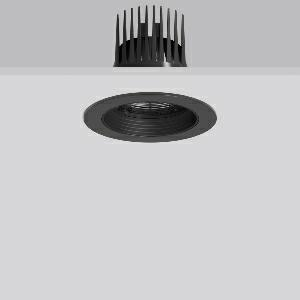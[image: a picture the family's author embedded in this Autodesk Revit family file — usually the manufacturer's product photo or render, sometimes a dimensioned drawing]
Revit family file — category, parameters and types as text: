
# Revit family: heledon_maxi_e_901767_003_1_8370
name_source: partatom
category: Lighting Fixtures
units: mm (PartAtom-declared; Revit-internal decimal feet)

## family parameters
Cut with Voids When Loaded = No
Host = Face
Light Source = No
Part Type = Normal
Room Calculation Point = No
Round Connector Dimension = Use Diameter
Shared = No

## types (1)
- HELEDON maxi E (1 x LED Modul 940, 3900 lm, 4000)
    Apparent Load = 35 VA
    Approval mark = CE
    CIE Flux Codes = 97 100 100 100 100
    Color Rendering = 92
    Color Temperature = 4000
    Default Elevation = 1800 mm
    Description = Series: HELEDON maxi
Round recessed downlight. Housing: die-cast aluminium, powder-coated. Black plastic ring and recessed LED to prevent glare from the side. Optical assembly with lens made of plastic (polycarbonate) for the best homogeneous light distribution - can be changed without tools. Best colour rendering index Ra>90. Suitable for Recessed ceiling mounting. Installation without tools thanks to spring fastening system. Including separate LED converter with connecting cable 600 mm.High quality converter without flickering and stroboscopic effect. Through-wiring box (5 pole) available as accessory. The following accessories can be mounted without use of tools: interchangeable lenses, decorative glasses, honeycomb louvre, clear and frosted diffusers, white interchangeable plastic ring. 
Colour: deep black, matt (RAL 9005)
Diameter: 162 mm
Height: 3 mm
Cut-out diameter: 152 mm
Recess height: 200 mm
Luminaire: recess height: 135 mm
Lamp: LED
Socket: without socket
Colour temperature: 4000K
Colour rendering index (CRI): 92
System power: 35 W
Rated luminous flux: 3900 lm
Luminous efficiency: 111 lm/W
Control gear: Regulated power supply
Protection class: II
Type of protection: IP 20
    Height = 0 mm  [stored 0 ft]
    Lamp = 1 x LED Modul 940
    Lamp Light Flux = 3900 lm
    Lamp count = 1
    Length = 162 mm
    Lifetime = 50000 h
    Luminous efficacy = 111 lm/W
    Manufacturer = RZB
    ModVariant = No
    Model = 901767.003.1
    Mounting Place = Ceiling
    Mounting Type = Recessed
    Number of Poles = 1
    OnlyDefault = Yes
    Power Factor = 1
    Product Name = HELEDON maxi E
    Product group = Recessed downlights
    ProductGroupID = 402
    Protection Class = Protection class II
    Protection Degree = IP 20
    RLX_Detail_Level = 1
    RLX_Emergency_Light_Flux = 0 lm
    RLX_Emergency_Type = 0
    RLX_Emergency_Type_DB = No
    RlxData = <blob elided: 122037 chars, md5=48b50c5d>
    Socket = socket
    Standby Power = 0 W
    System Light Flux = 3900 lm
    System Power = 35 W
    Type Comments = Product without accessories
    Type Image = 901663.003.jpg
    URL = http://relux.com
    VarID = ---
    Voltage = 230 V
    Voltage Range = 220-240 V
    Weight = 0.00 kg
    Width = 0 mm  [stored 0 ft]

note: [stored X ft] marks values corroborated as IEEE doubles in the binary element streams (Revit-internal decimal feet)

## geometry (parser evidence)
native form markers: Blend x4, Sweep x12
no freeform markers — native parametric forms only
